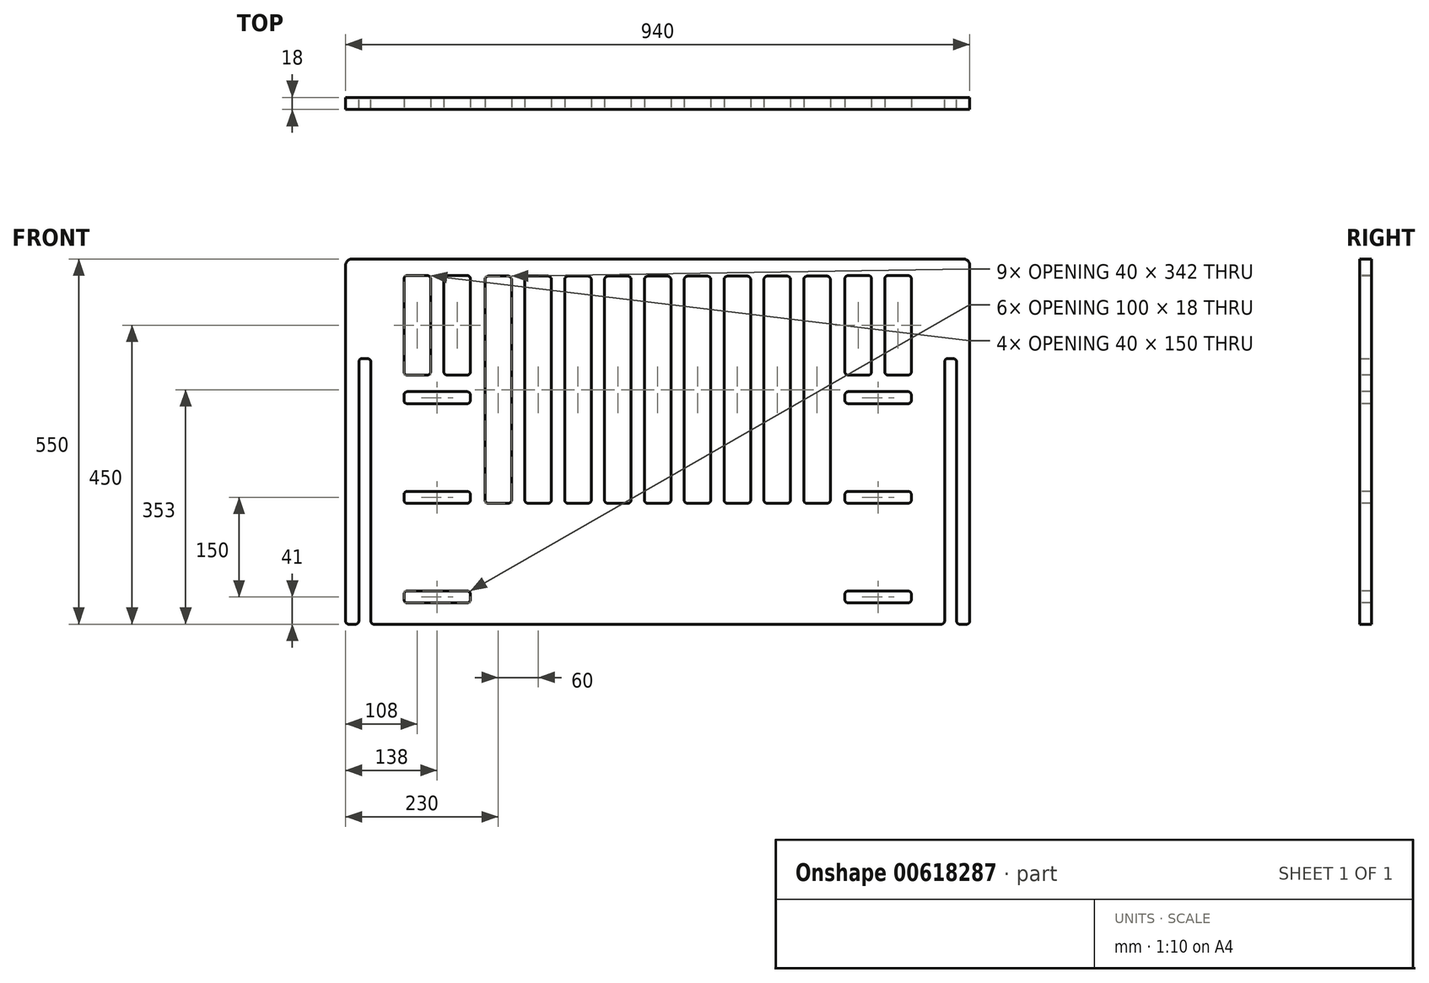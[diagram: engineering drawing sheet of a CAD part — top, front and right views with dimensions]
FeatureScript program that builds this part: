
annotation { "Feature Type Name" : "Feature", "Feature Type Description" : "" }
export const myFeature = defineFeature(function(context is Context, id is Id, definition is map)
    precondition{}
    {
        {
            var Q0;
            Q0=qCreatedBy(makeId("Front.planeOp"),FACE);
            var sketch = newSketch(context, id + "F0", { "sketchPlane" : qUnion([Q0])});
            skLineSegment(sketch, "E0", {"start": v(0, 0) * mm, "end": v(0, 550) * mm});
            skLineSegment(sketch, "E1", {"start": v(0, 550) * mm, "end": v(940, 550) * mm});
            skLineSegment(sketch, "E2", {"start": v(940, 550) * mm, "end": v(940, 0) * mm});
            skLineSegment(sketch, "E3", {"start": v(940, 0) * mm, "end": v(920, 0) * mm});
            skLineSegment(sketch, "E4", {"start": v(920, 0) * mm, "end": v(920, 400) * mm});
            skLineSegment(sketch, "E5", {"start": v(920, 400) * mm, "end": v(902, 400) * mm});
            skLineSegment(sketch, "E6", {"start": v(902, 400) * mm, "end": v(902, 0) * mm});
            skLineSegment(sketch, "E7", {"start": v(902, 0) * mm, "end": v(38, 0) * mm});
            skLineSegment(sketch, "E8", {"start": v(38, 0) * mm, "end": v(38, 400) * mm});
            skLineSegment(sketch, "E9", {"start": v(38, 400) * mm, "end": v(20, 400) * mm});
            skLineSegment(sketch, "E10", {"start": v(20, 400) * mm, "end": v(20, 0) * mm});
            skLineSegment(sketch, "E11", {"start": v(20, 0) * mm, "end": v(0, 0) * mm});
            skSolve(sketch);
        }
        {
            var Q0;
            Q0=makeQuery(id+"F0.imprint","IMPRINT",FACE,{"disambiguationData":[TD([[makeQuery(id+"F0.imprint","IMPRINT",EDGE,{"derivedFrom":sQuery(id+"F0.wireOp",EDGE,"E0")}),-1.0]])]});
            extrude(context, id + "F1", {"entities" : qUnion([Q0]), "depth" : 18 * mm, "offsetDistance" : 25 * mm});
        }
        {
            var Q0;
            Q0=makeQuery(id+"F1.opExtrude","CAP_FACE",FACE,{"disambiguationData":[OSD([sQuery(id+"F0.wireOp",EDGE,"E0"),sQuery(id+"F0.wireOp",EDGE,"E1"),sQuery(id+"F0.wireOp",EDGE,"E2"),sQuery(id+"F0.wireOp",EDGE,"E3"),sQuery(id+"F0.wireOp",EDGE,"E4"),sQuery(id+"F0.wireOp",EDGE,"E5"),sQuery(id+"F0.wireOp",EDGE,"E6"),sQuery(id+"F0.wireOp",EDGE,"E7"),sQuery(id+"F0.wireOp",EDGE,"E8"),sQuery(id+"F0.wireOp",EDGE,"E9"),sQuery(id+"F0.wireOp",EDGE,"E10"),sQuery(id+"F0.wireOp",EDGE,"E11")])],"isStart":false});
            var sketch = newSketch(context, id + "F2", { "sketchPlane" : qUnion([Q0])});
            skLineSegment(sketch, "E12.bottom", {"start": v(88, 350) * mm, "end": v(188, 350) * mm});
            skLineSegment(sketch, "E12.top", {"start": v(88, 332) * mm, "end": v(188, 332) * mm});
            skLineSegment(sketch, "E12.left", {"start": v(88, 350) * mm, "end": v(88, 332) * mm});
            skLineSegment(sketch, "E12.right", {"start": v(188, 350) * mm, "end": v(188, 332) * mm});
            skSolve(sketch);
        }
        {
            var Q0;
            Q0=makeQuery(id+"F2.imprint","IMPRINT",FACE,{"disambiguationData":[TD([[makeQuery(id+"F2.imprint","IMPRINT",EDGE,{"derivedFrom":sQuery(id+"F2.wireOp",EDGE,"E12.bottom")}),-1.0]])]});
            extrude(context, id + "F3", {"entities" : qUnion([Q0]), "operationType" : NewBodyOperationType.REMOVE, "oppositeDirection" : true, "depth" : 25 * mm, "offsetDistance" : 25 * mm});
        }
        {
            var Q0;
            Q0=makeQuery(id+"F1.opExtrude","CAP_FACE",FACE,{"disambiguationData":[OSD([sQuery(id+"F0.wireOp",EDGE,"E0"),sQuery(id+"F0.wireOp",EDGE,"E1"),sQuery(id+"F0.wireOp",EDGE,"E2"),sQuery(id+"F0.wireOp",EDGE,"E3"),sQuery(id+"F0.wireOp",EDGE,"E4"),sQuery(id+"F0.wireOp",EDGE,"E5"),sQuery(id+"F0.wireOp",EDGE,"E6"),sQuery(id+"F0.wireOp",EDGE,"E7"),sQuery(id+"F0.wireOp",EDGE,"E8"),sQuery(id+"F0.wireOp",EDGE,"E9"),sQuery(id+"F0.wireOp",EDGE,"E10"),sQuery(id+"F0.wireOp",EDGE,"E11")])],"isStart":false});
            var sketch = newSketch(context, id + "F4", { "sketchPlane" : qUnion([Q0])});
            skLineSegment(sketch, "E13.bottom", {"start": v(88, 200) * mm, "end": v(188, 200) * mm});
            skLineSegment(sketch, "E13.top", {"start": v(88, 182) * mm, "end": v(188, 182) * mm});
            skLineSegment(sketch, "E13.left", {"start": v(88, 200) * mm, "end": v(88, 182) * mm});
            skLineSegment(sketch, "E13.right", {"start": v(188, 200) * mm, "end": v(188, 182) * mm});
            skLineSegment(sketch, "E14.bottom", {"start": v(88, 50) * mm, "end": v(188, 50) * mm});
            skLineSegment(sketch, "E14.top", {"start": v(88, 32) * mm, "end": v(188, 32) * mm});
            skLineSegment(sketch, "E14.left", {"start": v(88, 50) * mm, "end": v(88, 32) * mm});
            skLineSegment(sketch, "E14.right", {"start": v(188, 50) * mm, "end": v(188, 32) * mm});
            skLineSegment(sketch, "E15.bottom", {"start": v(752, 350) * mm, "end": v(852, 350) * mm});
            skLineSegment(sketch, "E15.top", {"start": v(752, 332) * mm, "end": v(852, 332) * mm});
            skLineSegment(sketch, "E15.left", {"start": v(752, 350) * mm, "end": v(752, 332) * mm});
            skLineSegment(sketch, "E15.right", {"start": v(852, 350) * mm, "end": v(852, 332) * mm});
            skLineSegment(sketch, "E16.bottom", {"start": v(752, 200) * mm, "end": v(852, 200) * mm});
            skLineSegment(sketch, "E16.top", {"start": v(752, 182) * mm, "end": v(852, 182) * mm});
            skLineSegment(sketch, "E16.left", {"start": v(752, 200) * mm, "end": v(752, 182) * mm});
            skLineSegment(sketch, "E16.right", {"start": v(852, 200) * mm, "end": v(852, 182) * mm});
            skLineSegment(sketch, "E17.bottom", {"start": v(752, 50) * mm, "end": v(852, 50) * mm});
            skLineSegment(sketch, "E17.top", {"start": v(752, 32) * mm, "end": v(852, 32) * mm});
            skLineSegment(sketch, "E17.left", {"start": v(752, 50) * mm, "end": v(752, 32) * mm});
            skLineSegment(sketch, "E17.right", {"start": v(852, 50) * mm, "end": v(852, 32) * mm});
            skSolve(sketch);
        }
        {
            var Q0;
            Q0=makeQuery(id+"F4.imprint","IMPRINT",FACE,{"disambiguationData":[TD([[makeQuery(id+"F4.imprint","IMPRINT",EDGE,{"derivedFrom":sQuery(id+"F4.wireOp",EDGE,"E13.bottom")}),-1.0]])]});
            var Q1;
            Q1=makeQuery(id+"F4.imprint","IMPRINT",FACE,{"disambiguationData":[TD([[makeQuery(id+"F4.imprint","IMPRINT",EDGE,{"derivedFrom":sQuery(id+"F4.wireOp",EDGE,"E14.bottom")}),-1.0]])]});
            var Q2;
            Q2=makeQuery(id+"F4.imprint","IMPRINT",FACE,{"disambiguationData":[TD([[makeQuery(id+"F4.imprint","IMPRINT",EDGE,{"derivedFrom":sQuery(id+"F4.wireOp",EDGE,"E15.bottom")}),-1.0]])]});
            var Q3;
            Q3=makeQuery(id+"F4.imprint","IMPRINT",FACE,{"disambiguationData":[TD([[makeQuery(id+"F4.imprint","IMPRINT",EDGE,{"derivedFrom":sQuery(id+"F4.wireOp",EDGE,"E16.bottom")}),-1.0]])]});
            var Q4;
            Q4=makeQuery(id+"F4.imprint","IMPRINT",FACE,{"disambiguationData":[TD([[makeQuery(id+"F4.imprint","IMPRINT",EDGE,{"derivedFrom":sQuery(id+"F4.wireOp",EDGE,"E17.bottom")}),-1.0]])]});
            extrude(context, id + "F5", {"entities" : qUnion([Q0, Q1, Q2, Q3, Q4]), "operationType" : NewBodyOperationType.REMOVE, "oppositeDirection" : true, "depth" : 25 * mm, "offsetDistance" : 25 * mm});
        }
        {
            var Q0;
            Q0=makeQuery(id+"F1.opExtrude","SWEPT_EDGE",EDGE,{"disambiguationData":[OSD([sQuery(id+"F0.wireOp",EDGE,"E0"),sQuery(id+"F0.wireOp",EDGE,"E1")])]});
            var Q1;
            Q1=makeQuery(id+"F1.opExtrude","SWEPT_EDGE",EDGE,{"disambiguationData":[OSD([sQuery(id+"F0.wireOp",EDGE,"E1"),sQuery(id+"F0.wireOp",EDGE,"E2")])]});
            fillet(context, id + "F6", {"entities" : qUnion([Q0, Q1]), "radius" : 10 * mm, "tangentPropagation" : true, "allowEdgeOverflow" : false});
        }
        {
            var Q0;
            Q0=makeQuery(id+"F1.opExtrude","SWEPT_EDGE",EDGE,{"disambiguationData":[OSD([sQuery(id+"F0.wireOp",EDGE,"E2"),sQuery(id+"F0.wireOp",EDGE,"E3")])]});
            var Q1;
            Q1=makeQuery(id+"F1.opExtrude","SWEPT_EDGE",EDGE,{"disambiguationData":[OSD([sQuery(id+"F0.wireOp",EDGE,"E3"),sQuery(id+"F0.wireOp",EDGE,"E4")])]});
            var Q2;
            Q2=makeQuery(id+"F1.opExtrude","SWEPT_EDGE",EDGE,{"disambiguationData":[OSD([sQuery(id+"F0.wireOp",EDGE,"E6"),sQuery(id+"F0.wireOp",EDGE,"E7")])]});
            var Q3;
            Q3=makeQuery(id+"F1.opExtrude","SWEPT_EDGE",EDGE,{"disambiguationData":[OSD([sQuery(id+"F0.wireOp",EDGE,"E5"),sQuery(id+"F0.wireOp",EDGE,"E6")])]});
            var Q4;
            Q4=makeQuery(id+"F1.opExtrude","SWEPT_EDGE",EDGE,{"disambiguationData":[OSD([sQuery(id+"F0.wireOp",EDGE,"E4"),sQuery(id+"F0.wireOp",EDGE,"E5")])]});
            fillet(context, id + "F7", {"entities" : qUnion([Q0, Q1, Q2, Q3, Q4]), "radius" : 5 * mm, "tangentPropagation" : true, "allowEdgeOverflow" : false});
        }
        {
            var Q0;
            Q0=makeQuery(id+"F5.boolean.opBoolean","COPY",EDGE,{"derivedFrom":makeQuery(id+"F5.opExtrude","SWEPT_EDGE",EDGE,{"disambiguationData":[OSD([sQuery(id+"F4.wireOp",EDGE,"E17.bottom"),sQuery(id+"F4.wireOp",EDGE,"E17.right")])]})});
            var Q1;
            Q1=makeQuery(id+"F5.boolean.opBoolean","COPY",EDGE,{"derivedFrom":makeQuery(id+"F5.opExtrude","SWEPT_EDGE",EDGE,{"disambiguationData":[OSD([sQuery(id+"F4.wireOp",EDGE,"E17.top"),sQuery(id+"F4.wireOp",EDGE,"E17.right")])]})});
            var Q2;
            Q2=makeQuery(id+"F5.boolean.opBoolean","COPY",EDGE,{"derivedFrom":makeQuery(id+"F5.opExtrude","SWEPT_EDGE",EDGE,{"disambiguationData":[OSD([sQuery(id+"F4.wireOp",EDGE,"E17.top"),sQuery(id+"F4.wireOp",EDGE,"E17.left")])]})});
            var Q3;
            Q3=makeQuery(id+"F5.boolean.opBoolean","COPY",EDGE,{"derivedFrom":makeQuery(id+"F5.opExtrude","SWEPT_EDGE",EDGE,{"disambiguationData":[OSD([sQuery(id+"F4.wireOp",EDGE,"E17.bottom"),sQuery(id+"F4.wireOp",EDGE,"E17.left")])]})});
            fillet(context, id + "F8", {"entities" : qUnion([Q0, Q1, Q2, Q3]), "radius" : 5 * mm, "tangentPropagation" : true, "allowEdgeOverflow" : false});
        }
        {
            var Q0;
            Q0=makeQuery(id+"F5.boolean.opBoolean","COPY",EDGE,{"derivedFrom":makeQuery(id+"F5.opExtrude","SWEPT_EDGE",EDGE,{"disambiguationData":[OSD([sQuery(id+"F4.wireOp",EDGE,"E16.bottom"),sQuery(id+"F4.wireOp",EDGE,"E16.left")])]})});
            var Q1;
            Q1=makeQuery(id+"F5.boolean.opBoolean","COPY",EDGE,{"derivedFrom":makeQuery(id+"F5.opExtrude","SWEPT_EDGE",EDGE,{"disambiguationData":[OSD([sQuery(id+"F4.wireOp",EDGE,"E16.top"),sQuery(id+"F4.wireOp",EDGE,"E16.left")])]})});
            var Q2;
            Q2=makeQuery(id+"F5.boolean.opBoolean","COPY",EDGE,{"derivedFrom":makeQuery(id+"F5.opExtrude","SWEPT_EDGE",EDGE,{"disambiguationData":[OSD([sQuery(id+"F4.wireOp",EDGE,"E16.top"),sQuery(id+"F4.wireOp",EDGE,"E16.right")])]})});
            var Q3;
            Q3=makeQuery(id+"F5.boolean.opBoolean","COPY",EDGE,{"derivedFrom":makeQuery(id+"F5.opExtrude","SWEPT_EDGE",EDGE,{"disambiguationData":[OSD([sQuery(id+"F4.wireOp",EDGE,"E16.bottom"),sQuery(id+"F4.wireOp",EDGE,"E16.right")])]})});
            fillet(context, id + "F9", {"entities" : qUnion([Q0, Q1, Q2, Q3]), "radius" : 5 * mm, "tangentPropagation" : true, "allowEdgeOverflow" : false});
        }
        {
            var Q0;
            Q0=makeQuery(id+"F5.boolean.opBoolean","COPY",EDGE,{"derivedFrom":makeQuery(id+"F5.opExtrude","SWEPT_EDGE",EDGE,{"disambiguationData":[OSD([sQuery(id+"F4.wireOp",EDGE,"E15.bottom"),sQuery(id+"F4.wireOp",EDGE,"E15.right")])]})});
            var Q1;
            Q1=makeQuery(id+"F5.boolean.opBoolean","COPY",EDGE,{"derivedFrom":makeQuery(id+"F5.opExtrude","SWEPT_EDGE",EDGE,{"disambiguationData":[OSD([sQuery(id+"F4.wireOp",EDGE,"E15.top"),sQuery(id+"F4.wireOp",EDGE,"E15.right")])]})});
            var Q2;
            Q2=makeQuery(id+"F5.boolean.opBoolean","COPY",EDGE,{"derivedFrom":makeQuery(id+"F5.opExtrude","SWEPT_EDGE",EDGE,{"disambiguationData":[OSD([sQuery(id+"F4.wireOp",EDGE,"E15.top"),sQuery(id+"F4.wireOp",EDGE,"E15.left")])]})});
            var Q3;
            Q3=makeQuery(id+"F5.boolean.opBoolean","COPY",EDGE,{"derivedFrom":makeQuery(id+"F5.opExtrude","SWEPT_EDGE",EDGE,{"disambiguationData":[OSD([sQuery(id+"F4.wireOp",EDGE,"E15.bottom"),sQuery(id+"F4.wireOp",EDGE,"E15.left")])]})});
            fillet(context, id + "F10", {"entities" : qUnion([Q0, Q1, Q2, Q3]), "radius" : 5 * mm, "tangentPropagation" : true, "allowEdgeOverflow" : false});
        }
        {
            var Q0;
            Q0=makeQuery(id+"F1.opExtrude","SWEPT_EDGE",EDGE,{"disambiguationData":[OSD([sQuery(id+"F0.wireOp",EDGE,"E0"),sQuery(id+"F0.wireOp",EDGE,"E11")])]});
            var Q1;
            Q1=makeQuery(id+"F1.opExtrude","SWEPT_EDGE",EDGE,{"disambiguationData":[OSD([sQuery(id+"F0.wireOp",EDGE,"E10"),sQuery(id+"F0.wireOp",EDGE,"E11")])]});
            var Q2;
            Q2=makeQuery(id+"F1.opExtrude","SWEPT_EDGE",EDGE,{"disambiguationData":[OSD([sQuery(id+"F0.wireOp",EDGE,"E7"),sQuery(id+"F0.wireOp",EDGE,"E8")])]});
            var Q3;
            Q3=makeQuery(id+"F1.opExtrude","SWEPT_EDGE",EDGE,{"disambiguationData":[OSD([sQuery(id+"F0.wireOp",EDGE,"E8"),sQuery(id+"F0.wireOp",EDGE,"E9")])]});
            var Q4;
            Q4=makeQuery(id+"F1.opExtrude","SWEPT_EDGE",EDGE,{"disambiguationData":[OSD([sQuery(id+"F0.wireOp",EDGE,"E9"),sQuery(id+"F0.wireOp",EDGE,"E10")])]});
            fillet(context, id + "F11", {"entities" : qUnion([Q0, Q1, Q2, Q3, Q4]), "radius" : 5 * mm, "tangentPropagation" : true, "allowEdgeOverflow" : false});
        }
        {
            var Q0;
            Q0=makeQuery(id+"F3.boolean.opBoolean","COPY",EDGE,{"derivedFrom":makeQuery(id+"F3.opExtrude","SWEPT_EDGE",EDGE,{"disambiguationData":[OSD([sQuery(id+"F2.wireOp",EDGE,"E12.bottom"),sQuery(id+"F2.wireOp",EDGE,"E12.left")])]})});
            var Q1;
            Q1=makeQuery(id+"F3.boolean.opBoolean","COPY",EDGE,{"derivedFrom":makeQuery(id+"F3.opExtrude","SWEPT_EDGE",EDGE,{"disambiguationData":[OSD([sQuery(id+"F2.wireOp",EDGE,"E12.top"),sQuery(id+"F2.wireOp",EDGE,"E12.left")])]})});
            var Q2;
            Q2=makeQuery(id+"F3.boolean.opBoolean","COPY",EDGE,{"derivedFrom":makeQuery(id+"F3.opExtrude","SWEPT_EDGE",EDGE,{"disambiguationData":[OSD([sQuery(id+"F2.wireOp",EDGE,"E12.bottom"),sQuery(id+"F2.wireOp",EDGE,"E12.right")])]})});
            var Q3;
            Q3=makeQuery(id+"F3.boolean.opBoolean","COPY",EDGE,{"derivedFrom":makeQuery(id+"F3.opExtrude","SWEPT_EDGE",EDGE,{"disambiguationData":[OSD([sQuery(id+"F2.wireOp",EDGE,"E12.top"),sQuery(id+"F2.wireOp",EDGE,"E12.right")])]})});
            fillet(context, id + "F12", {"entities" : qUnion([Q0, Q1, Q2, Q3]), "radius" : 5 * mm, "tangentPropagation" : true, "allowEdgeOverflow" : false});
        }
        {
            var Q0;
            Q0=makeQuery(id+"F5.boolean.opBoolean","COPY",EDGE,{"derivedFrom":makeQuery(id+"F5.opExtrude","SWEPT_EDGE",EDGE,{"disambiguationData":[OSD([sQuery(id+"F4.wireOp",EDGE,"E13.top"),sQuery(id+"F4.wireOp",EDGE,"E13.right")])]})});
            var Q1;
            Q1=makeQuery(id+"F5.boolean.opBoolean","COPY",EDGE,{"derivedFrom":makeQuery(id+"F5.opExtrude","SWEPT_EDGE",EDGE,{"disambiguationData":[OSD([sQuery(id+"F4.wireOp",EDGE,"E13.bottom"),sQuery(id+"F4.wireOp",EDGE,"E13.right")])]})});
            var Q2;
            Q2=makeQuery(id+"F5.boolean.opBoolean","COPY",EDGE,{"derivedFrom":makeQuery(id+"F5.opExtrude","SWEPT_EDGE",EDGE,{"disambiguationData":[OSD([sQuery(id+"F4.wireOp",EDGE,"E13.bottom"),sQuery(id+"F4.wireOp",EDGE,"E13.left")])]})});
            var Q3;
            Q3=makeQuery(id+"F5.boolean.opBoolean","COPY",EDGE,{"derivedFrom":makeQuery(id+"F5.opExtrude","SWEPT_EDGE",EDGE,{"disambiguationData":[OSD([sQuery(id+"F4.wireOp",EDGE,"E13.top"),sQuery(id+"F4.wireOp",EDGE,"E13.left")])]})});
            fillet(context, id + "F13", {"entities" : qUnion([Q0, Q1, Q2, Q3]), "radius" : 5 * mm, "tangentPropagation" : true, "allowEdgeOverflow" : false});
        }
        {
            var Q0;
            Q0=makeQuery(id+"F5.boolean.opBoolean","COPY",EDGE,{"derivedFrom":makeQuery(id+"F5.opExtrude","SWEPT_EDGE",EDGE,{"disambiguationData":[OSD([sQuery(id+"F4.wireOp",EDGE,"E14.bottom"),sQuery(id+"F4.wireOp",EDGE,"E14.left")])]})});
            var Q1;
            Q1=makeQuery(id+"F5.boolean.opBoolean","COPY",EDGE,{"derivedFrom":makeQuery(id+"F5.opExtrude","SWEPT_EDGE",EDGE,{"disambiguationData":[OSD([sQuery(id+"F4.wireOp",EDGE,"E14.bottom"),sQuery(id+"F4.wireOp",EDGE,"E14.right")])]})});
            var Q2;
            Q2=makeQuery(id+"F5.boolean.opBoolean","COPY",EDGE,{"derivedFrom":makeQuery(id+"F5.opExtrude","SWEPT_EDGE",EDGE,{"disambiguationData":[OSD([sQuery(id+"F4.wireOp",EDGE,"E14.top"),sQuery(id+"F4.wireOp",EDGE,"E14.right")])]})});
            var Q3;
            Q3=makeQuery(id+"F5.boolean.opBoolean","COPY",EDGE,{"derivedFrom":makeQuery(id+"F5.opExtrude","SWEPT_EDGE",EDGE,{"disambiguationData":[OSD([sQuery(id+"F4.wireOp",EDGE,"E14.top"),sQuery(id+"F4.wireOp",EDGE,"E14.left")])]})});
            fillet(context, id + "F14", {"entities" : qUnion([Q0, Q1, Q2, Q3]), "radius" : 5 * mm, "tangentPropagation" : true, "allowEdgeOverflow" : false});
        }
        {
            var Q0;
            Q0=makeQuery(id+"F1.opExtrude","CAP_FACE",FACE,{"disambiguationData":[OSD([sQuery(id+"F0.wireOp",EDGE,"E0"),sQuery(id+"F0.wireOp",EDGE,"E1"),sQuery(id+"F0.wireOp",EDGE,"E2"),sQuery(id+"F0.wireOp",EDGE,"E3"),sQuery(id+"F0.wireOp",EDGE,"E4"),sQuery(id+"F0.wireOp",EDGE,"E5"),sQuery(id+"F0.wireOp",EDGE,"E6"),sQuery(id+"F0.wireOp",EDGE,"E7"),sQuery(id+"F0.wireOp",EDGE,"E8"),sQuery(id+"F0.wireOp",EDGE,"E9"),sQuery(id+"F0.wireOp",EDGE,"E10"),sQuery(id+"F0.wireOp",EDGE,"E11")])],"isStart":false});
            var sketch = newSketch(context, id + "F15", { "sketchPlane" : qUnion([Q0])});
            skLineSegment(sketch, "E18.bottom", {"start": v(93, 525) * mm, "end": v(123, 525) * mm});
            skLineSegment(sketch, "E18.top", {"start": v(93, 375) * mm, "end": v(123, 375) * mm});
            skLineSegment(sketch, "E18.left", {"start": v(88, 520) * mm, "end": v(88, 380) * mm});
            skLineSegment(sketch, "E18.right", {"start": v(128, 520) * mm, "end": v(128, 380) * mm});
            skPoint(sketch, "E19.visualSharp", {"position": v(88, 375) * mm});
            skArc(sketch, "E19.filletArc", {"start": v(88, 380) * mm, "mid": v(89.46, 376.46) * mm, "end": v(93, 375) * mm});
            skPoint(sketch, "E20.visualSharp", {"position": v(128, 375) * mm});
            skArc(sketch, "E20.filletArc", {"start": v(123, 375) * mm, "mid": v(126.54, 376.46) * mm, "end": v(128, 380) * mm});
            skPoint(sketch, "E21.visualSharp", {"position": v(128, 525) * mm});
            skArc(sketch, "E21.filletArc", {"start": v(128, 520) * mm, "mid": v(126.54, 523.54) * mm, "end": v(123, 525) * mm});
            skPoint(sketch, "E22.visualSharp", {"position": v(88, 525) * mm});
            skArc(sketch, "E22.filletArc", {"start": v(93, 525) * mm, "mid": v(89.46, 523.54) * mm, "end": v(88, 520) * mm});
            skPoint(sketch, "E23.1.0.0", {"position": v(188, 525) * mm});
            skLineSegment(sketch, "E23.1.0.1", {"start": v(148, 520) * mm, "end": v(148, 380) * mm});
            skArc(sketch, "E23.1.0.2", {"start": v(188, 520) * mm, "mid": v(186.54, 523.54) * mm, "end": v(183, 525) * mm});
            skPoint(sketch, "E23.1.0.3", {"position": v(148, 525) * mm});
            skArc(sketch, "E23.1.0.4", {"start": v(148, 380) * mm, "mid": v(149.46, 376.46) * mm, "end": v(153, 375) * mm});
            skArc(sketch, "E23.1.0.5", {"start": v(153, 525) * mm, "mid": v(149.46, 523.54) * mm, "end": v(148, 520) * mm});
            skArc(sketch, "E23.1.0.6", {"start": v(183, 375) * mm, "mid": v(186.54, 376.46) * mm, "end": v(188, 380) * mm});
            skLineSegment(sketch, "E23.1.0.7", {"start": v(153, 375) * mm, "end": v(183, 375) * mm});
            skLineSegment(sketch, "E23.1.0.8", {"start": v(153, 525) * mm, "end": v(183, 525) * mm});
            skPoint(sketch, "E23.1.0.9", {"position": v(188, 375) * mm});
            skPoint(sketch, "E23.1.0.10", {"position": v(148, 375) * mm});
            skLineSegment(sketch, "E23.1.0.11", {"start": v(188, 520) * mm, "end": v(188, 380) * mm});
            skLineSegment(sketch, "E23.direction1", {"start": v(88, 375) * mm, "end": v(148, 375) * mm, "construction": true});
            skPoint(sketch, "E24.1.0.0", {"position": v(752, 525) * mm});
            skArc(sketch, "E24.1.0.1", {"start": v(792, 520) * mm, "mid": v(790.54, 523.54) * mm, "end": v(787, 525) * mm});
            skLineSegment(sketch, "E24.1.0.2", {"start": v(812, 520) * mm, "end": v(812, 380) * mm});
            skPoint(sketch, "E24.1.0.3", {"position": v(812, 375) * mm});
            skPoint(sketch, "E24.1.0.4", {"position": v(852, 525) * mm});
            skArc(sketch, "E24.1.0.5", {"start": v(847, 375) * mm, "mid": v(850.54, 376.46) * mm, "end": v(852, 380) * mm});
            skPoint(sketch, "E24.1.0.6", {"position": v(792, 375) * mm});
            skArc(sketch, "E24.1.0.7", {"start": v(817, 525) * mm, "mid": v(813.46, 523.54) * mm, "end": v(812, 520) * mm});
            skArc(sketch, "E24.1.0.8", {"start": v(812, 380) * mm, "mid": v(813.46, 376.46) * mm, "end": v(817, 375) * mm});
            skPoint(sketch, "E24.1.0.9", {"position": v(792, 525) * mm});
            skLineSegment(sketch, "E24.1.0.10", {"start": v(792, 520) * mm, "end": v(792, 380) * mm});
            skLineSegment(sketch, "E24.1.0.11", {"start": v(757, 525) * mm, "end": v(787, 525) * mm});
            skLineSegment(sketch, "E24.1.0.12", {"start": v(817, 525) * mm, "end": v(847, 525) * mm});
            skArc(sketch, "E24.1.0.13", {"start": v(752, 380) * mm, "mid": v(753.46, 376.46) * mm, "end": v(757, 375) * mm});
            skLineSegment(sketch, "E24.1.0.14", {"start": v(752, 375) * mm, "end": v(812, 375) * mm, "construction": true});
            skPoint(sketch, "E24.1.0.15", {"position": v(752, 375) * mm});
            skLineSegment(sketch, "E24.1.0.16", {"start": v(752, 520) * mm, "end": v(752, 380) * mm});
            skArc(sketch, "E24.1.0.17", {"start": v(757, 525) * mm, "mid": v(753.46, 523.54) * mm, "end": v(752, 520) * mm});
            skLineSegment(sketch, "E24.1.0.18", {"start": v(757, 375) * mm, "end": v(787, 375) * mm});
            skArc(sketch, "E24.1.0.19", {"start": v(787, 375) * mm, "mid": v(790.54, 376.46) * mm, "end": v(792, 380) * mm});
            skLineSegment(sketch, "E24.1.0.20", {"start": v(852, 520) * mm, "end": v(852, 380) * mm});
            skPoint(sketch, "E24.1.0.21", {"position": v(812, 525) * mm});
            skArc(sketch, "E24.1.0.22", {"start": v(852, 520) * mm, "mid": v(850.54, 523.54) * mm, "end": v(847, 525) * mm});
            skLineSegment(sketch, "E24.1.0.23", {"start": v(817, 375) * mm, "end": v(847, 375) * mm});
            skPoint(sketch, "E24.1.0.24", {"position": v(852, 375) * mm});
            skLineSegment(sketch, "E24.direction1", {"start": v(88, 375) * mm, "end": v(752, 375) * mm, "construction": true});
            skSolve(sketch);
        }
        {
            var Q0;
            Q0=makeQuery(id+"F15.imprint","IMPRINT",FACE,{"disambiguationData":[TD([[makeQuery(id+"F15.imprint","IMPRINT",EDGE,{"derivedFrom":sQuery(id+"F15.wireOp",EDGE,"E18.bottom")}),-1.0]])]});
            var Q1;
            Q1=makeQuery(id+"F15.imprint","IMPRINT",FACE,{"disambiguationData":[TD([[makeQuery(id+"F15.imprint","IMPRINT",EDGE,{"derivedFrom":sQuery(id+"F15.wireOp",EDGE,"E23.1.0.1")}),1.0]])]});
            extrude(context, id + "F16", {"entities" : qUnion([Q0, Q1]), "operationType" : NewBodyOperationType.REMOVE, "oppositeDirection" : true, "depth" : 25 * mm, "offsetDistance" : 25 * mm});
        }
        {
            var Q0;
            Q0=makeQuery(id+"F15.imprint","IMPRINT",FACE,{"disambiguationData":[TD([[makeQuery(id+"F15.imprint","IMPRINT",EDGE,{"derivedFrom":sQuery(id+"F15.wireOp",EDGE,"E18.bottom")}),-1.0]])]});
            var Q1;
            Q1=makeQuery(id+"F15.imprint","IMPRINT",FACE,{"disambiguationData":[TD([[makeQuery(id+"F15.imprint","IMPRINT",EDGE,{"derivedFrom":sQuery(id+"F15.wireOp",EDGE,"E23.1.0.1")}),1.0]])]});
            var Q2;
            Q2=makeQuery(id+"F15.imprint","IMPRINT",FACE,{"disambiguationData":[TD([[makeQuery(id+"F15.imprint","IMPRINT",EDGE,{"derivedFrom":sQuery(id+"F15.wireOp",EDGE,"E24.1.0.2")}),1.0]])]});
            var Q3;
            Q3=makeQuery(id+"F15.imprint","IMPRINT",FACE,{"disambiguationData":[TD([[makeQuery(id+"F15.imprint","IMPRINT",EDGE,{"derivedFrom":sQuery(id+"F15.wireOp",EDGE,"E24.1.0.1")}),1.0]])]});
            extrude(context, id + "F17", {"entities" : qUnion([Q0, Q1, Q2, Q3]), "operationType" : NewBodyOperationType.REMOVE, "oppositeDirection" : true, "depth" : 25 * mm, "offsetDistance" : 25 * mm});
        }
        {
            var Q0;
            Q0=makeQuery(id+"F1.opExtrude","CAP_FACE",FACE,{"disambiguationData":[OSD([sQuery(id+"F0.wireOp",EDGE,"E0"),sQuery(id+"F0.wireOp",EDGE,"E1"),sQuery(id+"F0.wireOp",EDGE,"E2"),sQuery(id+"F0.wireOp",EDGE,"E3"),sQuery(id+"F0.wireOp",EDGE,"E4"),sQuery(id+"F0.wireOp",EDGE,"E5"),sQuery(id+"F0.wireOp",EDGE,"E6"),sQuery(id+"F0.wireOp",EDGE,"E7"),sQuery(id+"F0.wireOp",EDGE,"E8"),sQuery(id+"F0.wireOp",EDGE,"E9"),sQuery(id+"F0.wireOp",EDGE,"E10"),sQuery(id+"F0.wireOp",EDGE,"E11")])],"isStart":false});
            var sketch = newSketch(context, id + "F18", { "sketchPlane" : qUnion([Q0])});
            skLineSegment(sketch, "E25.bottom", {"start": v(215, 524) * mm, "end": v(245, 524) * mm});
            skLineSegment(sketch, "E25.top", {"start": v(215, 182) * mm, "end": v(245, 182) * mm});
            skLineSegment(sketch, "E25.left", {"start": v(210, 519) * mm, "end": v(210, 187) * mm});
            skLineSegment(sketch, "E25.right", {"start": v(250, 519) * mm, "end": v(250, 187) * mm});
            skPoint(sketch, "E26.visualSharp", {"position": v(210, 182) * mm});
            skArc(sketch, "E26.filletArc", {"start": v(210, 187) * mm, "mid": v(211.46, 183.46) * mm, "end": v(215, 182) * mm});
            skPoint(sketch, "E27.visualSharp", {"position": v(250, 182) * mm});
            skArc(sketch, "E27.filletArc", {"start": v(245, 182) * mm, "mid": v(248.54, 183.46) * mm, "end": v(250, 187) * mm});
            skPoint(sketch, "E28.visualSharp", {"position": v(250, 524) * mm});
            skArc(sketch, "E28.filletArc", {"start": v(250, 519) * mm, "mid": v(248.54, 522.54) * mm, "end": v(245, 524) * mm});
            skPoint(sketch, "E29.visualSharp", {"position": v(210, 524) * mm});
            skArc(sketch, "E29.filletArc", {"start": v(215, 524) * mm, "mid": v(211.46, 522.54) * mm, "end": v(210, 519) * mm});
            skLineSegment(sketch, "E30.1.0.0", {"start": v(275, 524) * mm, "end": v(305, 524) * mm});
            skLineSegment(sketch, "E30.1.0.1", {"start": v(270, 519) * mm, "end": v(270, 187) * mm});
            skPoint(sketch, "E30.1.0.2", {"position": v(270, 182) * mm});
            skPoint(sketch, "E30.1.0.3", {"position": v(310, 524) * mm});
            skPoint(sketch, "E30.1.0.4", {"position": v(310, 182) * mm});
            skLineSegment(sketch, "E30.1.0.5", {"start": v(275, 182) * mm, "end": v(305, 182) * mm});
            skArc(sketch, "E30.1.0.6", {"start": v(275, 524) * mm, "mid": v(271.46, 522.54) * mm, "end": v(270, 519) * mm});
            skPoint(sketch, "E30.1.0.7", {"position": v(270, 524) * mm});
            skArc(sketch, "E30.1.0.8", {"start": v(270, 187) * mm, "mid": v(271.46, 183.46) * mm, "end": v(275, 182) * mm});
            skArc(sketch, "E30.1.0.9", {"start": v(310, 519) * mm, "mid": v(308.54, 522.54) * mm, "end": v(305, 524) * mm});
            skArc(sketch, "E30.1.0.10", {"start": v(305, 182) * mm, "mid": v(308.54, 183.46) * mm, "end": v(310, 187) * mm});
            skLineSegment(sketch, "E30.1.0.11", {"start": v(310, 519) * mm, "end": v(310, 187) * mm});
            skLineSegment(sketch, "E30.2.0.0", {"start": v(335, 524) * mm, "end": v(365, 524) * mm});
            skLineSegment(sketch, "E30.2.0.1", {"start": v(330, 519) * mm, "end": v(330, 187) * mm});
            skPoint(sketch, "E30.2.0.2", {"position": v(330, 182) * mm});
            skPoint(sketch, "E30.2.0.3", {"position": v(370, 524) * mm});
            skPoint(sketch, "E30.2.0.4", {"position": v(370, 182) * mm});
            skLineSegment(sketch, "E30.2.0.5", {"start": v(335, 182) * mm, "end": v(365, 182) * mm});
            skArc(sketch, "E30.2.0.6", {"start": v(335, 524) * mm, "mid": v(331.46, 522.54) * mm, "end": v(330, 519) * mm});
            skPoint(sketch, "E30.2.0.7", {"position": v(330, 524) * mm});
            skArc(sketch, "E30.2.0.8", {"start": v(330, 187) * mm, "mid": v(331.46, 183.46) * mm, "end": v(335, 182) * mm});
            skArc(sketch, "E30.2.0.9", {"start": v(370, 519) * mm, "mid": v(368.54, 522.54) * mm, "end": v(365, 524) * mm});
            skArc(sketch, "E30.2.0.10", {"start": v(365, 182) * mm, "mid": v(368.54, 183.46) * mm, "end": v(370, 187) * mm});
            skLineSegment(sketch, "E30.2.0.11", {"start": v(370, 519) * mm, "end": v(370, 187) * mm});
            skLineSegment(sketch, "E30.3.0.0", {"start": v(395, 524) * mm, "end": v(425, 524) * mm});
            skLineSegment(sketch, "E30.3.0.1", {"start": v(390, 519) * mm, "end": v(390, 187) * mm});
            skPoint(sketch, "E30.3.0.2", {"position": v(390, 182) * mm});
            skPoint(sketch, "E30.3.0.3", {"position": v(430, 524) * mm});
            skPoint(sketch, "E30.3.0.4", {"position": v(430, 182) * mm});
            skLineSegment(sketch, "E30.3.0.5", {"start": v(395, 182) * mm, "end": v(425, 182) * mm});
            skArc(sketch, "E30.3.0.6", {"start": v(395, 524) * mm, "mid": v(391.46, 522.54) * mm, "end": v(390, 519) * mm});
            skPoint(sketch, "E30.3.0.7", {"position": v(390, 524) * mm});
            skArc(sketch, "E30.3.0.8", {"start": v(390, 187) * mm, "mid": v(391.46, 183.46) * mm, "end": v(395, 182) * mm});
            skArc(sketch, "E30.3.0.9", {"start": v(430, 519) * mm, "mid": v(428.54, 522.54) * mm, "end": v(425, 524) * mm});
            skArc(sketch, "E30.3.0.10", {"start": v(425, 182) * mm, "mid": v(428.54, 183.46) * mm, "end": v(430, 187) * mm});
            skLineSegment(sketch, "E30.3.0.11", {"start": v(430, 519) * mm, "end": v(430, 187) * mm});
            skLineSegment(sketch, "E30.4.0.0", {"start": v(455, 524) * mm, "end": v(485, 524) * mm});
            skLineSegment(sketch, "E30.4.0.1", {"start": v(450, 519) * mm, "end": v(450, 187) * mm});
            skPoint(sketch, "E30.4.0.2", {"position": v(450, 182) * mm});
            skPoint(sketch, "E30.4.0.3", {"position": v(490, 524) * mm});
            skPoint(sketch, "E30.4.0.4", {"position": v(490, 182) * mm});
            skLineSegment(sketch, "E30.4.0.5", {"start": v(455, 182) * mm, "end": v(485, 182) * mm});
            skArc(sketch, "E30.4.0.6", {"start": v(455, 524) * mm, "mid": v(451.46, 522.54) * mm, "end": v(450, 519) * mm});
            skPoint(sketch, "E30.4.0.7", {"position": v(450, 524) * mm});
            skArc(sketch, "E30.4.0.8", {"start": v(450, 187) * mm, "mid": v(451.46, 183.46) * mm, "end": v(455, 182) * mm});
            skArc(sketch, "E30.4.0.9", {"start": v(490, 519) * mm, "mid": v(488.54, 522.54) * mm, "end": v(485, 524) * mm});
            skArc(sketch, "E30.4.0.10", {"start": v(485, 182) * mm, "mid": v(488.54, 183.46) * mm, "end": v(490, 187) * mm});
            skLineSegment(sketch, "E30.4.0.11", {"start": v(490, 519) * mm, "end": v(490, 187) * mm});
            skLineSegment(sketch, "E30.5.0.0", {"start": v(515, 524) * mm, "end": v(545, 524) * mm});
            skLineSegment(sketch, "E30.5.0.1", {"start": v(510, 519) * mm, "end": v(510, 187) * mm});
            skPoint(sketch, "E30.5.0.2", {"position": v(510, 182) * mm});
            skPoint(sketch, "E30.5.0.3", {"position": v(550, 524) * mm});
            skPoint(sketch, "E30.5.0.4", {"position": v(550, 182) * mm});
            skLineSegment(sketch, "E30.5.0.5", {"start": v(515, 182) * mm, "end": v(545, 182) * mm});
            skArc(sketch, "E30.5.0.6", {"start": v(515, 524) * mm, "mid": v(511.46, 522.54) * mm, "end": v(510, 519) * mm});
            skPoint(sketch, "E30.5.0.7", {"position": v(510, 524) * mm});
            skArc(sketch, "E30.5.0.8", {"start": v(510, 187) * mm, "mid": v(511.46, 183.46) * mm, "end": v(515, 182) * mm});
            skArc(sketch, "E30.5.0.9", {"start": v(550, 519) * mm, "mid": v(548.54, 522.54) * mm, "end": v(545, 524) * mm});
            skArc(sketch, "E30.5.0.10", {"start": v(545, 182) * mm, "mid": v(548.54, 183.46) * mm, "end": v(550, 187) * mm});
            skLineSegment(sketch, "E30.5.0.11", {"start": v(550, 519) * mm, "end": v(550, 187) * mm});
            skLineSegment(sketch, "E30.6.0.0", {"start": v(575, 524) * mm, "end": v(605, 524) * mm});
            skLineSegment(sketch, "E30.6.0.1", {"start": v(570, 519) * mm, "end": v(570, 187) * mm});
            skPoint(sketch, "E30.6.0.2", {"position": v(570, 182) * mm});
            skPoint(sketch, "E30.6.0.3", {"position": v(610, 524) * mm});
            skPoint(sketch, "E30.6.0.4", {"position": v(610, 182) * mm});
            skLineSegment(sketch, "E30.6.0.5", {"start": v(575, 182) * mm, "end": v(605, 182) * mm});
            skArc(sketch, "E30.6.0.6", {"start": v(575, 524) * mm, "mid": v(571.46, 522.54) * mm, "end": v(570, 519) * mm});
            skPoint(sketch, "E30.6.0.7", {"position": v(570, 524) * mm});
            skArc(sketch, "E30.6.0.8", {"start": v(570, 187) * mm, "mid": v(571.46, 183.46) * mm, "end": v(575, 182) * mm});
            skArc(sketch, "E30.6.0.9", {"start": v(610, 519) * mm, "mid": v(608.54, 522.54) * mm, "end": v(605, 524) * mm});
            skArc(sketch, "E30.6.0.10", {"start": v(605, 182) * mm, "mid": v(608.54, 183.46) * mm, "end": v(610, 187) * mm});
            skLineSegment(sketch, "E30.6.0.11", {"start": v(610, 519) * mm, "end": v(610, 187) * mm});
            skLineSegment(sketch, "E30.7.0.0", {"start": v(635, 524) * mm, "end": v(665, 524) * mm});
            skLineSegment(sketch, "E30.7.0.1", {"start": v(630, 519) * mm, "end": v(630, 187) * mm});
            skPoint(sketch, "E30.7.0.2", {"position": v(630, 182) * mm});
            skPoint(sketch, "E30.7.0.3", {"position": v(670, 524) * mm});
            skPoint(sketch, "E30.7.0.4", {"position": v(670, 182) * mm});
            skLineSegment(sketch, "E30.7.0.5", {"start": v(635, 182) * mm, "end": v(665, 182) * mm});
            skArc(sketch, "E30.7.0.6", {"start": v(635, 524) * mm, "mid": v(631.46, 522.54) * mm, "end": v(630, 519) * mm});
            skPoint(sketch, "E30.7.0.7", {"position": v(630, 524) * mm});
            skArc(sketch, "E30.7.0.8", {"start": v(630, 187) * mm, "mid": v(631.46, 183.46) * mm, "end": v(635, 182) * mm});
            skArc(sketch, "E30.7.0.9", {"start": v(670, 519) * mm, "mid": v(668.54, 522.54) * mm, "end": v(665, 524) * mm});
            skArc(sketch, "E30.7.0.10", {"start": v(665, 182) * mm, "mid": v(668.54, 183.46) * mm, "end": v(670, 187) * mm});
            skLineSegment(sketch, "E30.7.0.11", {"start": v(670, 519) * mm, "end": v(670, 187) * mm});
            skLineSegment(sketch, "E30.8.0.0", {"start": v(695, 524) * mm, "end": v(725, 524) * mm});
            skLineSegment(sketch, "E30.8.0.1", {"start": v(690, 519) * mm, "end": v(690, 187) * mm});
            skPoint(sketch, "E30.8.0.2", {"position": v(690, 182) * mm});
            skPoint(sketch, "E30.8.0.3", {"position": v(730, 524) * mm});
            skPoint(sketch, "E30.8.0.4", {"position": v(730, 182) * mm});
            skLineSegment(sketch, "E30.8.0.5", {"start": v(695, 182) * mm, "end": v(725, 182) * mm});
            skArc(sketch, "E30.8.0.6", {"start": v(695, 524) * mm, "mid": v(691.46, 522.54) * mm, "end": v(690, 519) * mm});
            skPoint(sketch, "E30.8.0.7", {"position": v(690, 524) * mm});
            skArc(sketch, "E30.8.0.8", {"start": v(690, 187) * mm, "mid": v(691.46, 183.46) * mm, "end": v(695, 182) * mm});
            skArc(sketch, "E30.8.0.9", {"start": v(730, 519) * mm, "mid": v(728.54, 522.54) * mm, "end": v(725, 524) * mm});
            skArc(sketch, "E30.8.0.10", {"start": v(725, 182) * mm, "mid": v(728.54, 183.46) * mm, "end": v(730, 187) * mm});
            skLineSegment(sketch, "E30.8.0.11", {"start": v(730, 519) * mm, "end": v(730, 187) * mm});
            skLineSegment(sketch, "E30.direction1", {"start": v(210, 182) * mm, "end": v(270, 182) * mm, "construction": true});
            skSolve(sketch);
        }
        {
            var Q0;
            Q0=makeQuery(id+"F18.imprint","IMPRINT",FACE,{"disambiguationData":[TD([[makeQuery(id+"F18.imprint","IMPRINT",EDGE,{"derivedFrom":sQuery(id+"F18.wireOp",EDGE,"E25.bottom")}),-1.0]])]});
            var Q1;
            Q1=makeQuery(id+"F18.imprint","IMPRINT",FACE,{"disambiguationData":[TD([[makeQuery(id+"F18.imprint","IMPRINT",EDGE,{"derivedFrom":sQuery(id+"F18.wireOp",EDGE,"E30.3.0.0")}),-1.0]])]});
            var Q2;
            Q2=makeQuery(id+"F18.imprint","IMPRINT",FACE,{"disambiguationData":[TD([[makeQuery(id+"F18.imprint","IMPRINT",EDGE,{"derivedFrom":sQuery(id+"F18.wireOp",EDGE,"E30.8.0.0")}),-1.0]])]});
            var Q3;
            Q3=makeQuery(id+"F18.imprint","IMPRINT",FACE,{"disambiguationData":[TD([[makeQuery(id+"F18.imprint","IMPRINT",EDGE,{"derivedFrom":sQuery(id+"F18.wireOp",EDGE,"E30.1.0.0")}),-1.0]])]});
            var Q4;
            Q4=makeQuery(id+"F18.imprint","IMPRINT",FACE,{"disambiguationData":[TD([[makeQuery(id+"F18.imprint","IMPRINT",EDGE,{"derivedFrom":sQuery(id+"F18.wireOp",EDGE,"E30.2.0.0")}),-1.0]])]});
            var Q5;
            Q5=makeQuery(id+"F18.imprint","IMPRINT",FACE,{"disambiguationData":[TD([[makeQuery(id+"F18.imprint","IMPRINT",EDGE,{"derivedFrom":sQuery(id+"F18.wireOp",EDGE,"E30.4.0.0")}),-1.0]])]});
            var Q6;
            Q6=makeQuery(id+"F18.imprint","IMPRINT",FACE,{"disambiguationData":[TD([[makeQuery(id+"F18.imprint","IMPRINT",EDGE,{"derivedFrom":sQuery(id+"F18.wireOp",EDGE,"E30.5.0.0")}),-1.0]])]});
            var Q7;
            Q7=makeQuery(id+"F18.imprint","IMPRINT",FACE,{"disambiguationData":[TD([[makeQuery(id+"F18.imprint","IMPRINT",EDGE,{"derivedFrom":sQuery(id+"F18.wireOp",EDGE,"E30.6.0.0")}),-1.0]])]});
            var Q8;
            Q8=makeQuery(id+"F18.imprint","IMPRINT",FACE,{"disambiguationData":[TD([[makeQuery(id+"F18.imprint","IMPRINT",EDGE,{"derivedFrom":sQuery(id+"F18.wireOp",EDGE,"E30.7.0.0")}),-1.0]])]});
            extrude(context, id + "F19", {"entities" : qUnion([Q0, Q1, Q2, Q3, Q4, Q5, Q6, Q7, Q8]), "operationType" : NewBodyOperationType.REMOVE, "oppositeDirection" : true, "depth" : 25 * mm, "offsetDistance" : 25 * mm});
        }
    });
